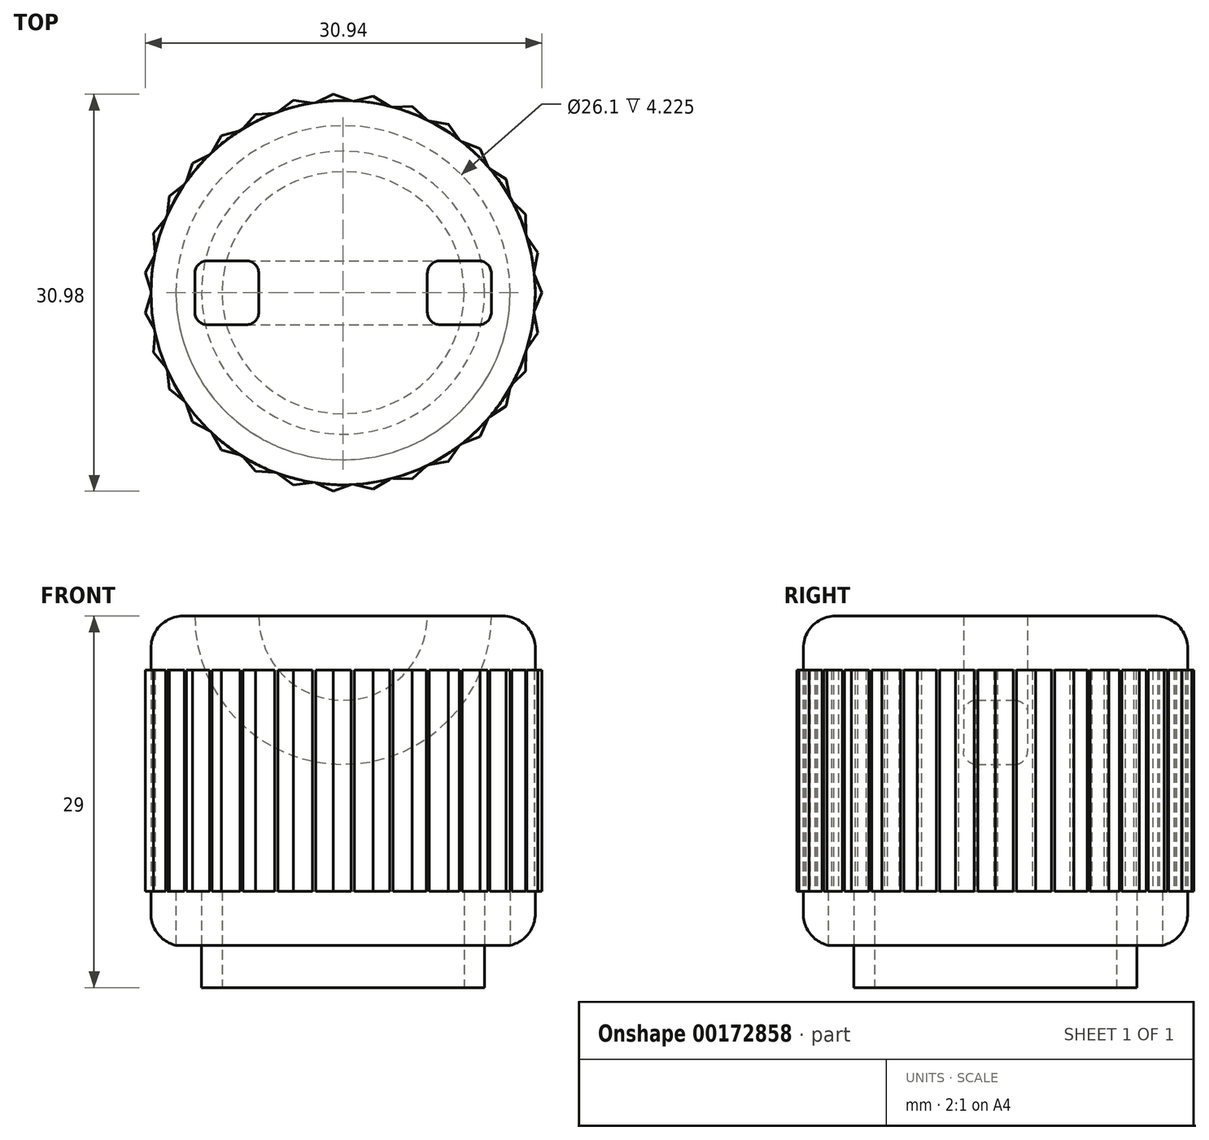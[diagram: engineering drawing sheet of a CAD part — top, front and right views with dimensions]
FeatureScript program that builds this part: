
annotation { "Feature Type Name" : "Feature", "Feature Type Description" : "" }
export const myFeature = defineFeature(function(context is Context, id is Id, definition is map)
    precondition{}
    {
        {
            var Q0;
            Q0=qCreatedBy(makeId("Top.planeOp"),FACE);
            var sketch = newSketch(context, id + "F0", { "sketchPlane" : qUnion([Q0])});
            skCircle(sketch, "E0", {"center": v(0, 0) * mm, "radius": 11.05 * mm});
            skCircle(sketch, "E1.0", {"center": v(0, 0) * mm, "radius": 9.45 * mm});
            skCircle(sketch, "E2.0", {"center": v(0, 0) * mm, "radius": 13.05 * mm});
            skCircle(sketch, "E3.0", {"center": v(0, 0) * mm, "radius": 15 * mm});
            skSolve(sketch);
        }
        {
            var Q0;
            Q0=makeQuery(id+"F0.imprint","IMPRINT",FACE,{"disambiguationData":[TD([[makeQuery(id+"F0.imprint","IMPRINT",EDGE,{"derivedFrom":sQuery(id+"F0.wireOp",EDGE,"E0")}),1.0]])]});
            extrude(context, id + "F1", {"entities" : qUnion([Q0]), "endBound" : BoundingType.SYMMETRIC, "depth" : 9 * mm});
        }
        {
            var Q0;
            Q0=makeQuery(id+"F1.opExtrude","CAP_FACE",FACE,{"disambiguationData":[OSD([sQuery(id+"F0.wireOp",EDGE,"E0"),sQuery(id+"F0.wireOp",EDGE,"E1.0"),sQuery(id+"F0.wireOp",EDGE,"KMxVIuWJ-jdXU-8mUH-ExQa-rNt1xYYHk3Ug"),sQuery(id+"F0.wireOp",EDGE,"d95f2093-270d-4cd6-8a94-b8cefc29fcbc0.MirrorCS")])],"isStart":false});
            cPlane(context, id + "F2", {"entities" : qUnion([Q0]), "cplaneType" : CPlaneType.OFFSET, "offset" : 0 * mm, "width" : 150 * mm, "height" : 150 * mm});
        }
        {
            var Q0;
            Q0=qCreatedBy(id+"F2.planeOp",FACE);
            var sketch = newSketch(context, id + "F3", { "sketchPlane" : qUnion([Q0])});
            skCircle(sketch, "E4", {"center": v(0, 0) * mm, "radius": 15 * mm});
            skSolve(sketch);
        }
        {
            var Q0;
            Q0=makeQuery(id+"F3.imprint","IMPRINT",FACE,{"disambiguationData":[TD([[makeQuery(id+"F3.imprint","IMPRINT",EDGE,{"derivedFrom":sQuery(id+"F3.wireOp",EDGE,"E4")}),1.0]])]});
            extrude(context, id + "F4", {"entities" : qUnion([Q0]), "operationType" : NewBodyOperationType.ADD, "depth" : 20 * mm});
        }
        {
            var Q0;
            Q0=qCreatedBy(makeId("Front.planeOp"),FACE);
            var sketch = newSketch(context, id + "F5", { "sketchPlane" : qUnion([Q0])});
            skArc(sketch, "E5", {"start": v(11.58, 24.5) * mm, "mid": v(0, 12.92) * mm, "end": v(-11.58, 24.5) * mm});
            skArc(sketch, "E6.0", {"start": v(6.58, 24.5) * mm, "mid": v(0, 17.92) * mm, "end": v(-6.58, 24.5) * mm});
            skLineSegment(sketch, "E7", {"start": v(-11.58, 24.5) * mm, "end": v(-6.58, 24.5) * mm});
            skLineSegment(sketch, "E8", {"start": v(6.58, 24.5) * mm, "end": v(11.58, 24.5) * mm});
            skSolve(sketch);
        }
        {
            var Q0;
            Q0=qCreatedBy(makeId("Top.planeOp"),FACE);
            cPlane(context, id + "F6", {"entities" : qUnion([Q0]), "cplaneType" : CPlaneType.OFFSET, "offset" : 11.65 * mm, "width" : 150 * mm, "height" : 150 * mm});
        }
        {
            var Q0;
            Q0=qCreatedBy(id+"F6.planeOp",FACE);
            var sketch = newSketch(context, id + "F7", { "sketchPlane" : qUnion([Q0])});
            skCircle(sketch, "E9", {"center": v(0, 0) * mm, "radius": 15 * mm});
            skLineSegment(sketch, "E10", {"start": v(15, 0) * mm, "end": v(15.5, 0) * mm, "construction": true});
            skLineSegment(sketch, "E11", {"start": v(15.5, 0) * mm, "end": v(14.94, -1.39) * mm});
            skLineSegment(sketch, "E12.MirrorCS", {"start": v(15.5, 0) * mm, "end": v(14.94, 1.39) * mm});
            skLineSegment(sketch, "E13.1.0", {"start": v(15.2, 3.12) * mm, "end": v(14.9, 1.65) * mm});
            skLineSegment(sketch, "E13.1.1", {"start": v(15.2, 3.12) * mm, "end": v(14.35, 4.36) * mm});
            skLineSegment(sketch, "E13.2.0", {"start": v(14.25, 6.12) * mm, "end": v(14.27, 4.62) * mm});
            skLineSegment(sketch, "E13.2.1", {"start": v(14.25, 6.12) * mm, "end": v(13.18, 7.16) * mm});
            skLineSegment(sketch, "E13.3.0", {"start": v(12.73, 8.86) * mm, "end": v(13.05, 7.4) * mm});
            skLineSegment(sketch, "E13.3.1", {"start": v(12.73, 8.86) * mm, "end": v(11.47, 9.67) * mm});
            skLineSegment(sketch, "E13.4.0", {"start": v(10.69, 11.24) * mm, "end": v(11.3, 9.87) * mm});
            skLineSegment(sketch, "E13.4.1", {"start": v(10.69, 11.24) * mm, "end": v(9.29, 11.78) * mm});
            skLineSegment(sketch, "E13.5.0", {"start": v(8.2, 13.16) * mm, "end": v(9.08, 11.94) * mm});
            skLineSegment(sketch, "E13.5.1", {"start": v(8.2, 13.16) * mm, "end": v(6.72, 13.4) * mm});
            skLineSegment(sketch, "E13.6.0", {"start": v(5.39, 14.54) * mm, "end": v(6.49, 13.52) * mm});
            skLineSegment(sketch, "E13.6.1", {"start": v(5.39, 14.54) * mm, "end": v(3.89, 14.49) * mm});
            skLineSegment(sketch, "E13.7.0", {"start": v(2.35, 15.33) * mm, "end": v(3.63, 14.55) * mm});
            skLineSegment(sketch, "E13.7.1", {"start": v(2.35, 15.33) * mm, "end": v(0.9, 14.97) * mm});
            skLineSegment(sketch, "E13.8.0", {"start": v(-0.79, 15.49) * mm, "end": v(0.63, 14.99) * mm});
            skLineSegment(sketch, "E13.8.1", {"start": v(-0.79, 15.49) * mm, "end": v(-2.14, 14.85) * mm});
            skLineSegment(sketch, "E13.9.0", {"start": v(-3.89, 15.01) * mm, "end": v(-2.4, 14.8) * mm});
            skLineSegment(sketch, "E13.9.1", {"start": v(-3.89, 15.01) * mm, "end": v(-5.08, 14.11) * mm});
            skLineSegment(sketch, "E13.10.0", {"start": v(-6.83, 13.92) * mm, "end": v(-5.33, 14.02) * mm});
            skLineSegment(sketch, "E13.10.1", {"start": v(-6.83, 13.92) * mm, "end": v(-7.82, 12.8) * mm});
            skLineSegment(sketch, "E13.11.0", {"start": v(-9.5, 12.26) * mm, "end": v(-8.05, 12.66) * mm});
            skLineSegment(sketch, "E13.11.1", {"start": v(-9.5, 12.26) * mm, "end": v(-10.24, 10.96) * mm});
            skLineSegment(sketch, "E13.12.0", {"start": v(-11.77, 10.1) * mm, "end": v(-10.43, 10.78) * mm});
            skLineSegment(sketch, "E13.12.1", {"start": v(-11.77, 10.1) * mm, "end": v(-12.24, 8.68) * mm});
            skLineSegment(sketch, "E13.13.0", {"start": v(-13.56, 7.53) * mm, "end": v(-12.39, 8.46) * mm});
            skLineSegment(sketch, "E13.13.1", {"start": v(-13.56, 7.53) * mm, "end": v(-13.73, 6.04) * mm});
            skLineSegment(sketch, "E13.14.0", {"start": v(-14.8, 4.64) * mm, "end": v(-13.84, 5.8) * mm});
            skLineSegment(sketch, "E13.14.1", {"start": v(-14.8, 4.64) * mm, "end": v(-14.67, 3.15) * mm});
            skLineSegment(sketch, "E13.15.0", {"start": v(-15.43, 1.57) * mm, "end": v(-14.72, 2.89) * mm});
            skLineSegment(sketch, "E13.15.1", {"start": v(-15.43, 1.57) * mm, "end": v(-15, 0.13) * mm});
            skLineSegment(sketch, "E13.16.0", {"start": v(-15.43, -1.57) * mm, "end": v(-15, -0.13) * mm});
            skLineSegment(sketch, "E13.16.1", {"start": v(-15.43, -1.57) * mm, "end": v(-14.72, -2.89) * mm});
            skLineSegment(sketch, "E13.17.0", {"start": v(-14.8, -4.64) * mm, "end": v(-14.67, -3.15) * mm});
            skLineSegment(sketch, "E13.17.1", {"start": v(-14.8, -4.64) * mm, "end": v(-13.84, -5.8) * mm});
            skLineSegment(sketch, "E13.18.0", {"start": v(-13.56, -7.53) * mm, "end": v(-13.73, -6.04) * mm});
            skLineSegment(sketch, "E13.18.1", {"start": v(-13.56, -7.53) * mm, "end": v(-12.39, -8.46) * mm});
            skLineSegment(sketch, "E13.19.0", {"start": v(-11.77, -10.1) * mm, "end": v(-12.24, -8.68) * mm});
            skLineSegment(sketch, "E13.19.1", {"start": v(-11.77, -10.1) * mm, "end": v(-10.43, -10.78) * mm});
            skLineSegment(sketch, "E13.20.0", {"start": v(-9.5, -12.26) * mm, "end": v(-10.24, -10.96) * mm});
            skLineSegment(sketch, "E13.20.1", {"start": v(-9.5, -12.26) * mm, "end": v(-8.05, -12.66) * mm});
            skLineSegment(sketch, "E13.21.0", {"start": v(-6.83, -13.92) * mm, "end": v(-7.82, -12.8) * mm});
            skLineSegment(sketch, "E13.21.1", {"start": v(-6.83, -13.92) * mm, "end": v(-5.33, -14.02) * mm});
            skLineSegment(sketch, "E13.22.0", {"start": v(-3.89, -15.01) * mm, "end": v(-5.08, -14.11) * mm});
            skLineSegment(sketch, "E13.22.1", {"start": v(-3.89, -15.01) * mm, "end": v(-2.4, -14.8) * mm});
            skLineSegment(sketch, "E13.23.0", {"start": v(-0.79, -15.49) * mm, "end": v(-2.14, -14.85) * mm});
            skLineSegment(sketch, "E13.23.1", {"start": v(-0.79, -15.49) * mm, "end": v(0.63, -14.99) * mm});
            skLineSegment(sketch, "E13.24.0", {"start": v(2.35, -15.33) * mm, "end": v(0.9, -14.97) * mm});
            skLineSegment(sketch, "E13.24.1", {"start": v(2.35, -15.33) * mm, "end": v(3.63, -14.55) * mm});
            skLineSegment(sketch, "E13.25.0", {"start": v(5.39, -14.54) * mm, "end": v(3.89, -14.49) * mm});
            skLineSegment(sketch, "E13.25.1", {"start": v(5.39, -14.54) * mm, "end": v(6.49, -13.52) * mm});
            skLineSegment(sketch, "E13.26.0", {"start": v(8.2, -13.16) * mm, "end": v(6.72, -13.4) * mm});
            skLineSegment(sketch, "E13.26.1", {"start": v(8.2, -13.16) * mm, "end": v(9.08, -11.94) * mm});
            skLineSegment(sketch, "E13.27.0", {"start": v(10.69, -11.24) * mm, "end": v(9.29, -11.78) * mm});
            skLineSegment(sketch, "E13.27.1", {"start": v(10.69, -11.24) * mm, "end": v(11.3, -9.87) * mm});
            skLineSegment(sketch, "E13.28.0", {"start": v(12.73, -8.86) * mm, "end": v(11.47, -9.67) * mm});
            skLineSegment(sketch, "E13.28.1", {"start": v(12.73, -8.86) * mm, "end": v(13.05, -7.4) * mm});
            skLineSegment(sketch, "E13.29.0", {"start": v(14.25, -6.12) * mm, "end": v(13.18, -7.16) * mm});
            skLineSegment(sketch, "E13.29.1", {"start": v(14.25, -6.12) * mm, "end": v(14.27, -4.62) * mm});
            skLineSegment(sketch, "E13.30.0", {"start": v(15.2, -3.12) * mm, "end": v(14.35, -4.36) * mm});
            skLineSegment(sketch, "E13.30.1", {"start": v(15.2, -3.12) * mm, "end": v(14.9, -1.65) * mm});
            skSolve(sketch);
        }
        {
            var Q0;
            Q0 = qSketchRegion(id + "F7", true);
            extrude(context, id + "F8", {"entities" : qUnion([Q0]), "operationType" : NewBodyOperationType.ADD, "endBound" : BoundingType.SYMMETRIC, "depth" : 17.25 * mm});
        }
        {
            var Q0;
            Q0 = qSketchRegion(id + "F5", true);
            extrude(context, id + "F9", {"entities" : qUnion([Q0]), "operationType" : NewBodyOperationType.REMOVE, "endBound" : BoundingType.SYMMETRIC, "depth" : 5 * mm});
        }
        {
            var Q0;
            Q0=makeQuery(id+"F9.boolean.opBoolean","COPY",EDGE,{"derivedFrom":makeQuery(id+"F9.opExtrude","CAP_EDGE",EDGE,{"disambiguationData":[OSD([sQuery(id+"F5.wireOp",EDGE,"E7")])],"isStart":true})});
            var Q1;
            Q1=makeQuery(id+"F9.boolean.opBoolean","COPY",EDGE,{"derivedFrom":makeQuery(id+"F9.opExtrude","SWEPT_EDGE",EDGE,{"disambiguationData":[OSD([sQuery(id+"F5.wireOp",EDGE,"E5"),sQuery(id+"F5.wireOp",EDGE,"E7")])]})});
            var Q2;
            Q2=makeQuery(id+"F9.boolean.opBoolean","COPY",EDGE,{"derivedFrom":makeQuery(id+"F9.opExtrude","CAP_EDGE",EDGE,{"disambiguationData":[OSD([sQuery(id+"F5.wireOp",EDGE,"E7")])],"isStart":false})});
            var Q3;
            Q3=makeQuery(id+"F9.boolean.opBoolean","COPY",EDGE,{"derivedFrom":makeQuery(id+"F9.opExtrude","SWEPT_EDGE",EDGE,{"disambiguationData":[OSD([sQuery(id+"F5.wireOp",EDGE,"E6.0"),sQuery(id+"F5.wireOp",EDGE,"E7")])]})});
            var Q4;
            Q4=makeQuery(id+"F9.boolean.opBoolean","COPY",EDGE,{"derivedFrom":makeQuery(id+"F9.opExtrude","CAP_EDGE",EDGE,{"disambiguationData":[OSD([sQuery(id+"F5.wireOp",EDGE,"E8")])],"isStart":true})});
            var Q5;
            Q5=makeQuery(id+"F9.boolean.opBoolean","COPY",EDGE,{"derivedFrom":makeQuery(id+"F9.opExtrude","SWEPT_EDGE",EDGE,{"disambiguationData":[OSD([sQuery(id+"F5.wireOp",EDGE,"E6.0"),sQuery(id+"F5.wireOp",EDGE,"E8")])]})});
            var Q6;
            Q6=makeQuery(id+"F9.boolean.opBoolean","COPY",EDGE,{"derivedFrom":makeQuery(id+"F9.opExtrude","SWEPT_EDGE",EDGE,{"disambiguationData":[OSD([sQuery(id+"F5.wireOp",EDGE,"E5"),sQuery(id+"F5.wireOp",EDGE,"E8")])]})});
            var Q7;
            Q7=makeQuery(id+"F9.boolean.opBoolean","COPY",EDGE,{"derivedFrom":makeQuery(id+"F9.opExtrude","CAP_EDGE",EDGE,{"disambiguationData":[OSD([sQuery(id+"F5.wireOp",EDGE,"E8")])],"isStart":false})});
            var Q8;
            Q8=makeQuery(id+"F9.boolean.opBoolean","COPY",EDGE,{"derivedFrom":makeQuery(id+"F9.opExtrude","CAP_EDGE",EDGE,{"disambiguationData":[OSD([sQuery(id+"F5.wireOp",EDGE,"E6.0")])],"isStart":true})});
            var Q9;
            Q9=makeQuery(id+"F9.boolean.opBoolean","COPY",EDGE,{"derivedFrom":makeQuery(id+"F9.opExtrude","CAP_EDGE",EDGE,{"disambiguationData":[OSD([sQuery(id+"F5.wireOp",EDGE,"E6.0")])],"isStart":false})});
            var Q10;
            Q10=makeQuery(id+"F9.boolean.opBoolean","COPY",EDGE,{"derivedFrom":makeQuery(id+"F9.opExtrude","CAP_EDGE",EDGE,{"disambiguationData":[OSD([sQuery(id+"F5.wireOp",EDGE,"E5")])],"isStart":false})});
            var Q11;
            Q11=makeQuery(id+"F9.boolean.opBoolean","COPY",EDGE,{"derivedFrom":makeQuery(id+"F9.opExtrude","CAP_EDGE",EDGE,{"disambiguationData":[OSD([sQuery(id+"F5.wireOp",EDGE,"E5")])],"isStart":true})});
            fillet(context, id + "F10", {"entities" : qUnion([Q0, Q1, Q2, Q3, Q4, Q5, Q6, Q7, Q8, Q9, Q10, Q11]), "radius" : 1 * mm, "tangentPropagation" : true, "allowEdgeOverflow" : false});
        }
        {
            var Q0;
            Q0=makeQuery(id+"F4.opExtrude","CAP_EDGE",EDGE,{"disambiguationData":[OSD([sQuery(id+"F3.wireOp",EDGE,"E4")])],"isStart":false});
            fillet(context, id + "F11", {"entities" : qUnion([Q0]), "radius" : 2.5 * mm, "tangentPropagation" : true, "allowEdgeOverflow" : false});
        }
        {
            var Q0;
            Q0=makeQuery(id+"F0.imprint","IMPRINT",FACE,{"disambiguationData":[TD([[makeQuery(id+"F0.imprint","IMPRINT",EDGE,{"derivedFrom":sQuery(id+"F0.wireOp",EDGE,"E2.0")}),-1.0]])]});
            extrude(context, id + "F12", {"entities" : qUnion([Q0]), "operationType" : NewBodyOperationType.ADD, "endBound" : BoundingType.UP_TO_NEXT, "depth" : 5 * mm});
        }
        {
            var Q0;
            Q0=makeQuery(id+"F0.imprint","IMPRINT",FACE,{"disambiguationData":[TD([[makeQuery(id+"F0.imprint","IMPRINT",EDGE,{"derivedFrom":sQuery(id+"F0.wireOp",EDGE,"E2.0")}),-1.0]])]});
            extrude(context, id + "F13", {"entities" : qUnion([Q0]), "operationType" : NewBodyOperationType.ADD, "oppositeDirection" : true, "depth" : 1.2 * mm});
        }
        {
            var Q0;
            Q0=makeQuery(id+"F13.opExtrude","CAP_EDGE",EDGE,{"disambiguationData":[OSD([sQuery(id+"F0.wireOp",EDGE,"E3.0")])],"isStart":false});
            fillet(context, id + "F14", {"entities" : qUnion([Q0]), "radius" : 2.5 * mm, "tangentPropagation" : true, "allowEdgeOverflow" : false});
        }
    });
